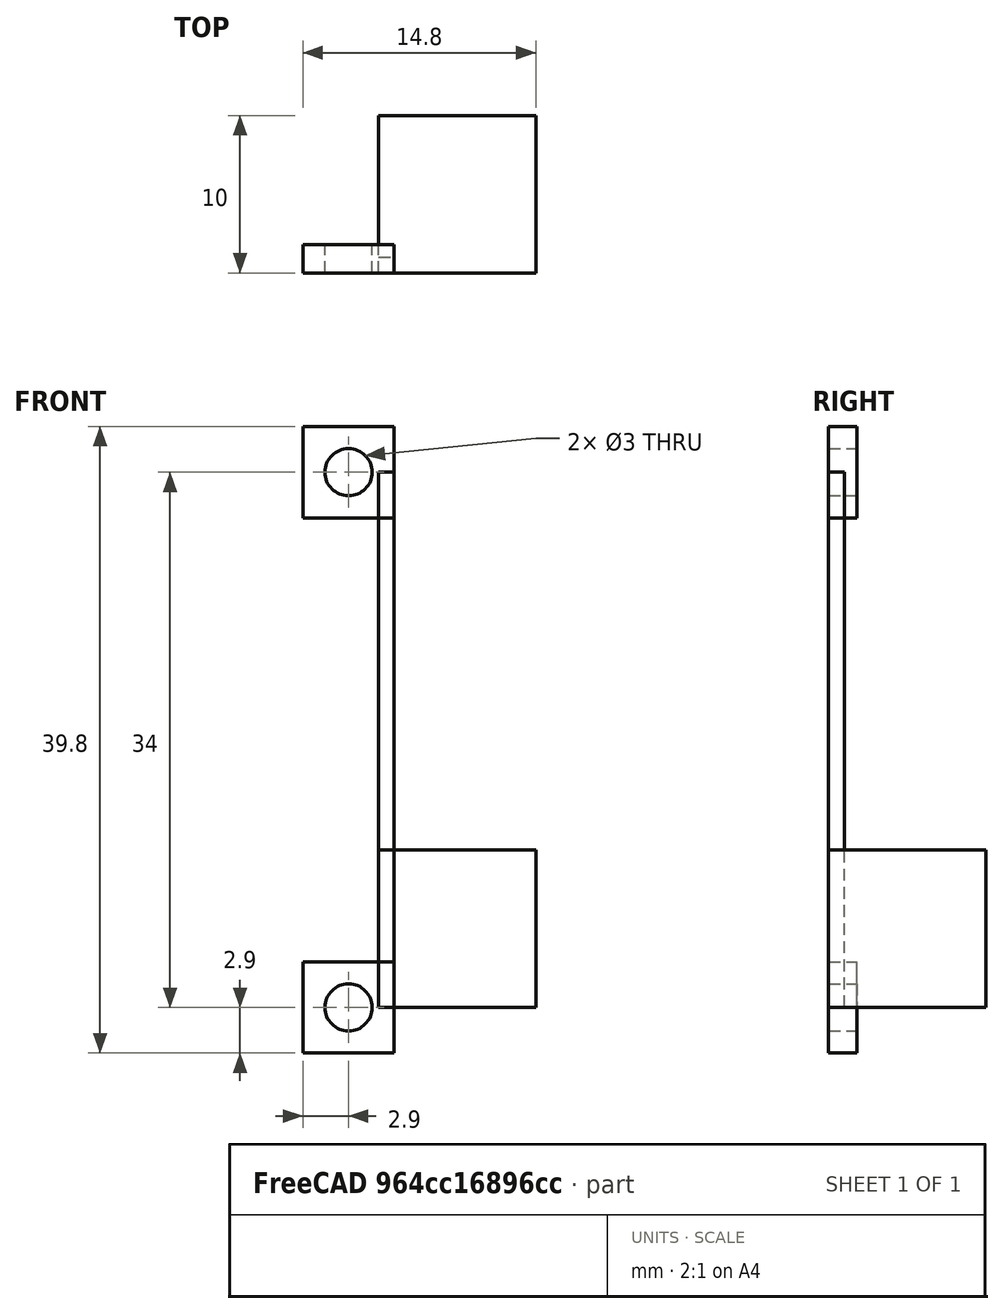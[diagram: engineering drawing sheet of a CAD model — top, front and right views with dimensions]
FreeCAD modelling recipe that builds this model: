
FCSTD DOCUMENT  (FreeCAD 0.18R14555 (Git shallow))
Label: hemera-proble-mount
License: All rights reserved
LicenseURL: http://en.wikipedia.org/wiki/All_rights_reserved
objects: Part::Box×4, Part::Cylinder×2, Part::Cut×2, Part::MultiFuse×1
note: 9 computed .brp shape members not serialized (recipe doc carries the construction recipe); baked Part::Feature solids carry a one-line shape summary decoded from their .brp

FEATURE [Part::Box] Box  label="Cube"
  AttacherType = Attacher::AttachEngine3D
  Height = 34
  Length = 1
  Width = 1
FEATURE [Part::Box] Box001  label="Cube001"
  AttacherType = Attacher::AttachEngine3D
  Height = 5.8
  Length = 5.8
  Placement = pos=(-2.9,0,-2.9) rot=(0,0,1;0rad)
  Width = 1.8
FEATURE [Part::Box] Box002  label="Cube002"
  AttacherType = Attacher::AttachEngine3D
  Height = 5.8
  Length = 5.8
  Placement = pos=(-2.9,0,31.1) rot=(0,0,1;0rad)
  Width = 1.8
FEATURE [Part::Cylinder] Cylinder
  Angle = 360
  AttacherType = Attacher::AttachEngine3D
  Height = 1.8
  Placement = pos=(0,0,0) rot=(1,0,0;4.71239rad)
  Radius = 1.5
FEATURE [Part::Cylinder] Cylinder001
  Angle = 360
  AttacherType = Attacher::AttachEngine3D
  Height = 1.8
  Placement = pos=(0,-7.5e-15,34) rot=(-1,0,0;1.5708rad)
  Radius = 1.5
FEATURE [Part::Cut] Cut
  Base = -> Box002
  Tool = -> Cylinder001
FEATURE [Part::Cut] Cut001
  Base = -> Box001
  Tool = -> Cylinder
FEATURE [Part::MultiFuse] Fusion
  Placement = pos=(-1.9,0,0) rot=(0,0,1;0rad)
  Shapes = -> [Cut,Cut001]
FEATURE [Part::Box] Box003  label="Cube003"
  AttacherType = Attacher::AttachEngine3D
  Height = 10
  Length = 10
  Width = 10
